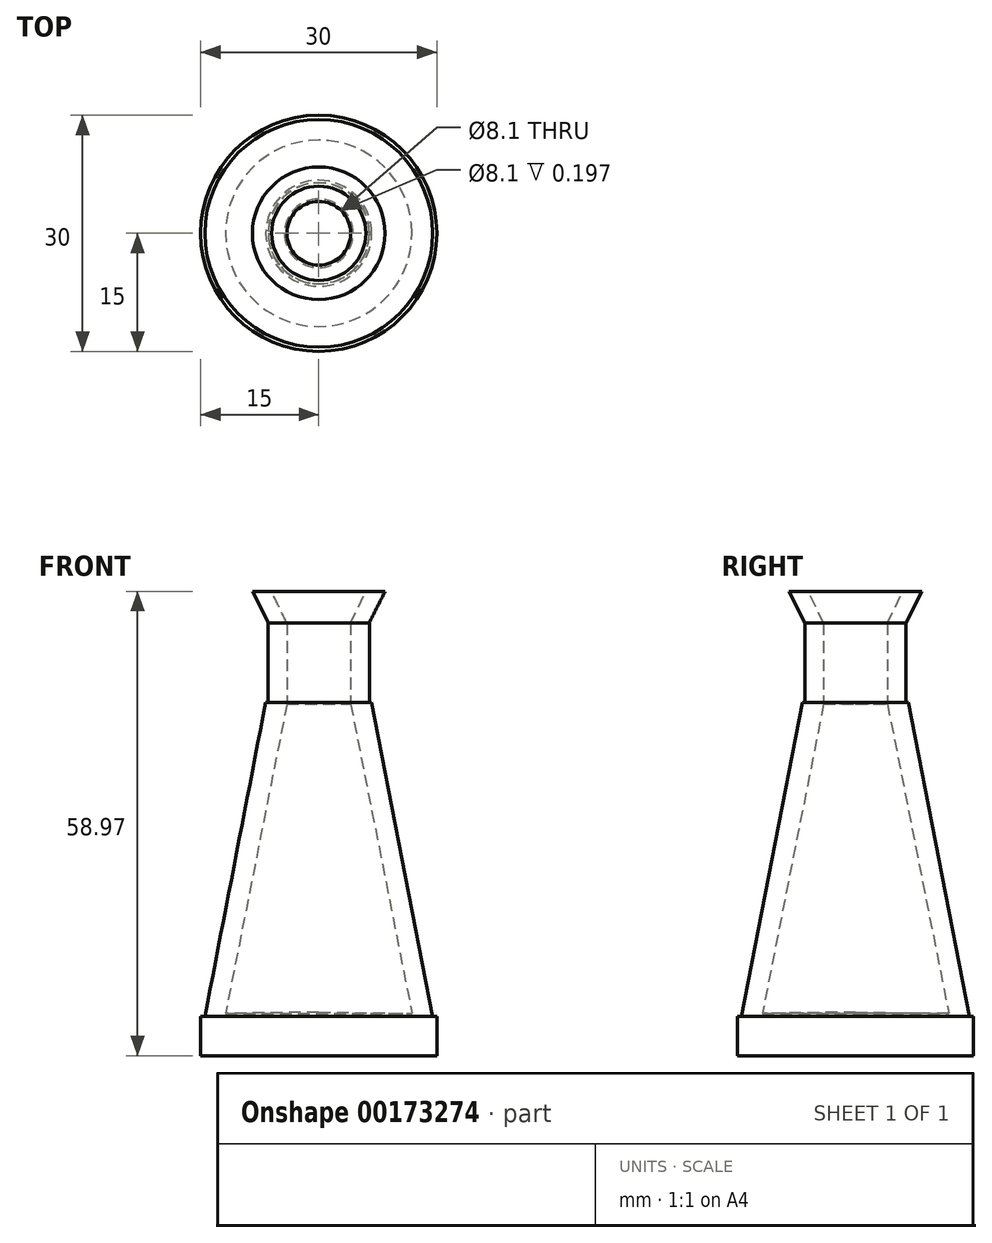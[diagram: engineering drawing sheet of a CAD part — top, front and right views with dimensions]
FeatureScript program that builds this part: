
annotation { "Feature Type Name" : "Feature", "Feature Type Description" : "" }
export const myFeature = defineFeature(function(context is Context, id is Id, definition is map)
    precondition{}
    {
        {
            var Q0;
            Q0=qCreatedBy(makeId("Top.planeOp"),FACE);
            var sketch = newSketch(context, id + "F0", { "sketchPlane" : qUnion([Q0])});
            skCircle(sketch, "E0", {"center": v(0, 0) * mm, "radius": 15 * mm});
            skSolve(sketch);
        }
        {
            var Q0;
            Q0=makeQuery(id+"F0.imprint","IMPRINT",FACE,{"disambiguationData":[TD([[makeQuery(id+"F0.imprint","IMPRINT",EDGE,{"derivedFrom":sQuery(id+"F0.wireOp",EDGE,"E0")}),1.0]])]});
            extrude(context, id + "F1", {"entities" : qUnion([Q0]), "depth" : 5 * mm});
        }
        {
            var Q0;
            Q0=qCreatedBy(makeId("Front.planeOp"),FACE);
            var sketch = newSketch(context, id + "F2", { "sketchPlane" : qUnion([Q0])});
            skLineSegment(sketch, "E1", {"start": v(0, 4.86) * mm, "end": v(0, 44.86) * mm});
            skLineSegment(sketch, "E2", {"start": v(0, 44.86) * mm, "end": v(-6.73, 44.86) * mm});
            skLineSegment(sketch, "E3", {"start": v(-6.73, 44.86) * mm, "end": v(-14.5, 4.86) * mm});
            skLineSegment(sketch, "E4", {"start": v(-14.5, 4.86) * mm, "end": v(0, 4.86) * mm});
            skSolve(sketch);
        }
        {
            var Q0;
            Q0=makeQuery(id+"F2.imprint","IMPRINT",FACE,{"disambiguationData":[TD([[makeQuery(id+"F2.imprint","IMPRINT",EDGE,{"derivedFrom":sQuery(id+"F2.wireOp",EDGE,"E1")}),1.0]])]});
            var Q1;
            Q1=sQuery(id+"F2.wireOp",EDGE,"E1");
            revolve(context, id + "F3", {"operationType" : NewBodyOperationType.ADD, "entities" : qUnion([Q0]), "axis" : qUnion([Q1]), "revolveType" : RevolveType.FULL});
        }
        {
            var Q0;
            Q0=qCreatedBy(makeId("Front.planeOp"),FACE);
            var sketch = newSketch(context, id + "F4", { "sketchPlane" : qUnion([Q0])});
            skLineSegment(sketch, "E5", {"start": v(0, 44.98) * mm, "end": v(0, 54.98) * mm});
            skLineSegment(sketch, "E6", {"start": v(0, 54.98) * mm, "end": v(-6.43, 54.98) * mm});
            skLineSegment(sketch, "E7", {"start": v(-6.43, 54.98) * mm, "end": v(-6.42, 44.8) * mm});
            skLineSegment(sketch, "E8", {"start": v(-6.42, 44.8) * mm, "end": v(0, 44.98) * mm});
            skSolve(sketch);
        }
        {
            var Q0;
            Q0=makeQuery(id+"F4.imprint","IMPRINT",FACE,{"disambiguationData":[TD([[makeQuery(id+"F4.imprint","IMPRINT",EDGE,{"derivedFrom":sQuery(id+"F4.wireOp",EDGE,"E5")}),1.0]])]});
            var Q1;
            Q1=sQuery(id+"F4.wireOp",EDGE,"E5");
            revolve(context, id + "F5", {"operationType" : NewBodyOperationType.ADD, "entities" : qUnion([Q0]), "axis" : qUnion([Q1]), "revolveType" : RevolveType.FULL});
        }
        {
            var Q0;
            Q0=qCreatedBy(makeId("Front.planeOp"),FACE);
            var sketch = newSketch(context, id + "F6", { "sketchPlane" : qUnion([Q0])});
            skLineSegment(sketch, "E9", {"start": v(-6.39, 54.97) * mm, "end": v(-8.43, 58.97) * mm});
            skLineSegment(sketch, "E10", {"start": v(-8.43, 58.97) * mm, "end": v(0, 58.97) * mm});
            skLineSegment(sketch, "E11", {"start": v(0, 58.97) * mm, "end": v(0, 54.97) * mm});
            skLineSegment(sketch, "E12", {"start": v(0, 54.97) * mm, "end": v(-6.39, 54.97) * mm});
            skSolve(sketch);
        }
        {
            var Q0;
            Q0=makeQuery(id+"F6.imprint","IMPRINT",FACE,{"disambiguationData":[TD([[makeQuery(id+"F6.imprint","IMPRINT",EDGE,{"derivedFrom":sQuery(id+"F6.wireOp",EDGE,"E9")}),-1.0]])]});
            var Q1;
            Q1=sQuery(id+"F6.wireOp",EDGE,"E11");
            revolve(context, id + "F7", {"operationType" : NewBodyOperationType.ADD, "entities" : qUnion([Q0]), "axis" : qUnion([Q1]), "revolveType" : RevolveType.FULL});
        }
        {
            var Q0;
            Q0=qCreatedBy(makeId("Front.planeOp"),FACE);
            var sketch = newSketch(context, id + "F8", { "sketchPlane" : qUnion([Q0])});
            skLineSegment(sketch, "E13", {"start": v(-11.84, 5.36) * mm, "end": v(-4.05, 44.67) * mm});
            skLineSegment(sketch, "E14", {"start": v(-4.05, 44.67) * mm, "end": v(-4.05, 54.95) * mm});
            skLineSegment(sketch, "E15", {"start": v(-4.05, 54.95) * mm, "end": v(-6.18, 59.37) * mm});
            skLineSegment(sketch, "E16", {"start": v(-6.18, 59.37) * mm, "end": v(0, 59.37) * mm});
            skLineSegment(sketch, "E17", {"start": v(0, 59.37) * mm, "end": v(0, 5.53) * mm});
            skLineSegment(sketch, "E18", {"start": v(0, 5.53) * mm, "end": v(-11.84, 5.36) * mm});
            skSolve(sketch);
        }
        {
            var Q0;
            Q0 = qSketchRegion(id + "F8", true);
            var Q1;
            Q1=sQuery(id+"F8.wireOp",EDGE,"E17");
            revolve(context, id + "F9", {"operationType" : NewBodyOperationType.REMOVE, "entities" : qUnion([Q0]), "axis" : qUnion([Q1]), "revolveType" : RevolveType.FULL, "oppositeDirection" : true});
        }
    });
